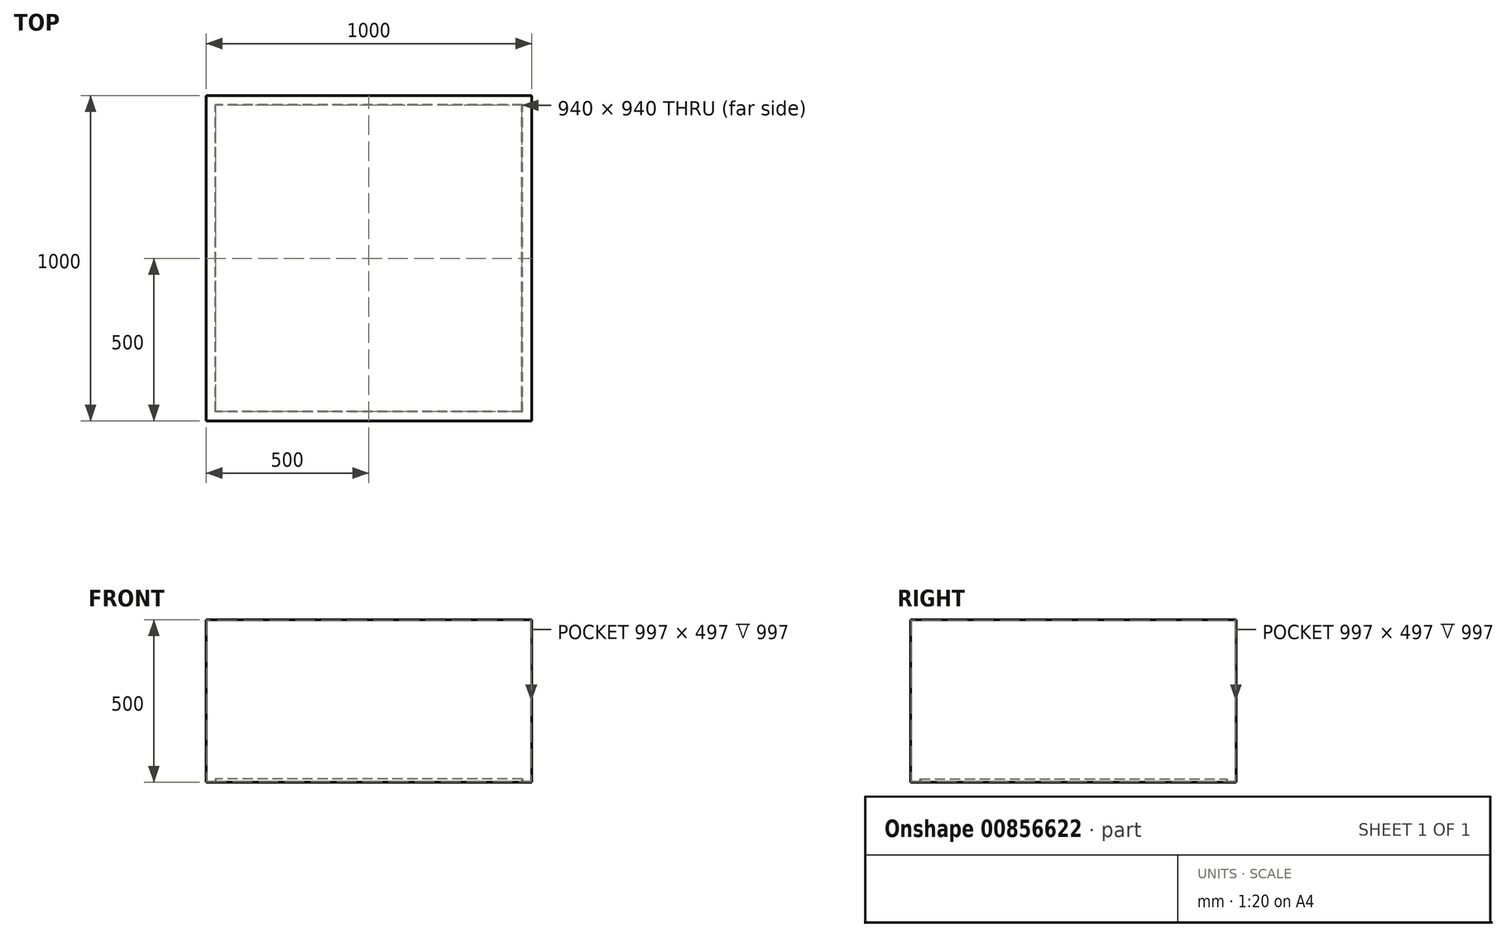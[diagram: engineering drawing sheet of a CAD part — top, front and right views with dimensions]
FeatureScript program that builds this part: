
annotation { "Feature Type Name" : "Feature", "Feature Type Description" : "" }
export const myFeature = defineFeature(function(context is Context, id is Id, definition is map)
    precondition{}
    {
        {
            var Q0;
            Q0=qCreatedBy(makeId("Top.planeOp"),FACE);
            var sketch = newSketch(context, id + "F0", { "sketchPlane" : qUnion([Q0])});
            skLineSegment(sketch, "E0.bottom", {"start": v(500, 500) * mm, "end": v(-500, 500) * mm});
            skLineSegment(sketch, "E0.top", {"start": v(500, -500) * mm, "end": v(-500, -500) * mm});
            skLineSegment(sketch, "E0.left", {"start": v(500, 500) * mm, "end": v(500, -500) * mm});
            skLineSegment(sketch, "E0.right", {"start": v(-500, 500) * mm, "end": v(-500, -500) * mm});
            skPoint(sketch, "E0.middle", {"position": v(0, 0) * mm});
            skSolve(sketch);
        }
        {
            var Q0;
            Q0 = qSketchRegion(id + "F0", true);
            extrude(context, id + "F1", {"entities" : qUnion([Q0]), "depth" : 500 * mm, "offsetDistance" : 25 * mm});
        }
        {
            var Q0;
            Q0=makeQuery(id+"F1.opExtrude","CAP_FACE",FACE,{"disambiguationData":[OSD([sQuery(id+"F0.wireOp",EDGE,"E0.bottom"),sQuery(id+"F0.wireOp",EDGE,"E0.top"),sQuery(id+"F0.wireOp",EDGE,"E0.left"),sQuery(id+"F0.wireOp",EDGE,"E0.right")])],"isStart":true});
            var sketch = newSketch(context, id + "F2", { "sketchPlane" : qUnion([Q0])});
            skLineSegment(sketch, "E1.bottom", {"start": v(470, 470) * mm, "end": v(-470, 470) * mm});
            skLineSegment(sketch, "E1.top", {"start": v(470, -470) * mm, "end": v(-470, -470) * mm});
            skLineSegment(sketch, "E1.left", {"start": v(470, 470) * mm, "end": v(470, -470) * mm});
            skLineSegment(sketch, "E1.right", {"start": v(-470, 470) * mm, "end": v(-470, -470) * mm});
            skPoint(sketch, "E1.middle", {"position": v(0, 0) * mm});
            skSolve(sketch);
        }
        {
            var Q0;
            Q0 = qSketchRegion(id + "F2", true);
            extrude(context, id + "F3", {"entities" : qUnion([Q0]), "operationType" : NewBodyOperationType.REMOVE, "oppositeDirection" : true, "depth" : 10 * mm, "offsetDistance" : 25 * mm});
        }
        {
            var Q0;
            Q0=makeQuery(id+"F3.boolean.opBoolean","COPY",FACE,{"derivedFrom":makeQuery(id+"F3.opExtrude","CAP_FACE",FACE,{"disambiguationData":[OSD([sQuery(id+"F2.wireOp",EDGE,"E1.bottom"),sQuery(id+"F2.wireOp",EDGE,"E1.top"),sQuery(id+"F2.wireOp",EDGE,"E1.left"),sQuery(id+"F2.wireOp",EDGE,"E1.right")])],"isStart":false})});
            shell(context, id + "F4", {"entities" : qUnion([Q0]), "thickness" : 1.5 * mm});
        }
    });
